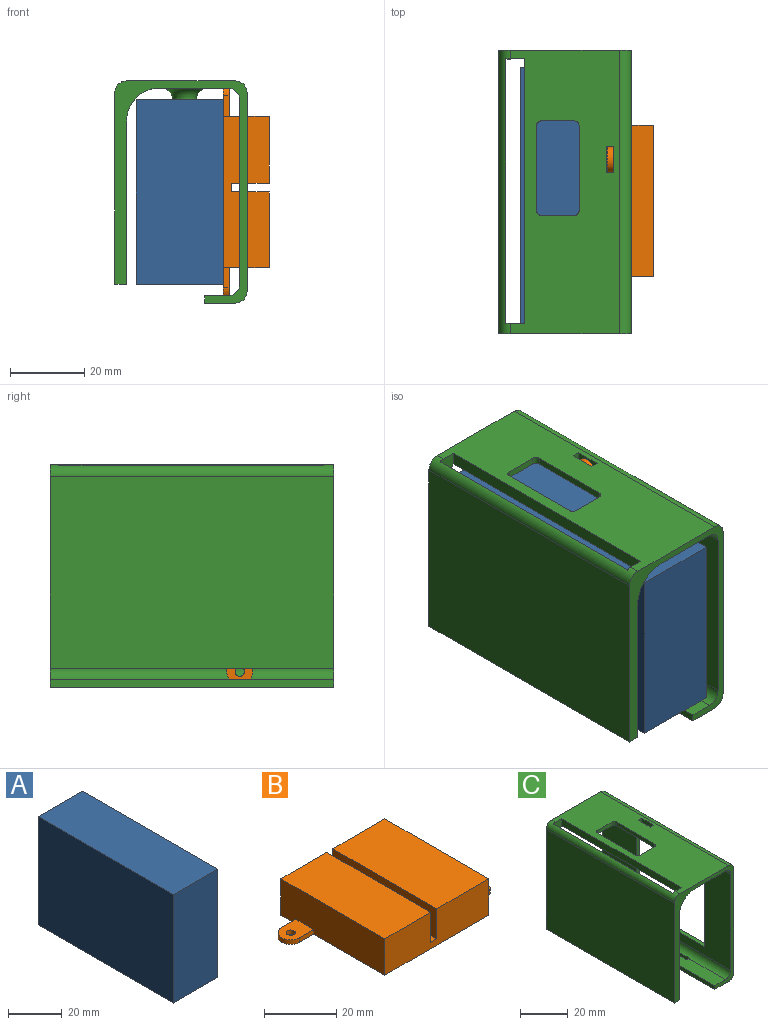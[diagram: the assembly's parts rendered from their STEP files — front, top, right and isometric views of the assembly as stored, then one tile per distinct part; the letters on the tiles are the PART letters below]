
ASSEMBLY  parts=3 mates=6
PART A: 6 faces, bbox 23.5x71.5x49.5 mm
  f0: plane 71.5x23.5mm, normal (0,0,-1), area 1679.9mm2, adj f1,f3,f4,f5
  f1: plane 71.5x49.53mm, normal (1,0,0), area 3541.4mm2, adj f0,f2,f4,f5
  f2: plane 71.5x23.5mm, normal (0,0,1), area 1679.9mm2, adj f1,f3,f4,f5
  f3: plane 71.5x49.53mm, normal (-1,0,0), area 3541.4mm2, adj f0,f2,f4,f5
  f4: plane 49.53x23.5mm, normal (0,-1,0), area 1163.7mm2, adj f0,f1,f2,f3
  f5: plane 49.53x23.5mm, normal (0,1,0), area 1163.7mm2, adj f0,f1,f2,f3
PART B: 20 faces, bbox 58.5x40.6x12.3 mm
  f0: plane 40.64x20.32mm, normal (0,0,1), area 825.8mm2, adj f1,f2,f3,f16
  f1: plane 40.64x12.32mm, normal (0,-1,0), area 476.7mm2, adj f0,f2,f4,f5,f6,f15,f16,f17
  f2: plane 40.64x12.32mm, normal (1,0,0), area 490mm2, adj f0,f1,f3,f6,f7,f8,f10
  f3: plane 40.64x12.32mm, normal (0,1,0), area 476.7mm2, adj f0,f2,f4,f5,f6,f15,f16,f17
  f4: plane 40.64x12.32mm, normal (-1,0,0), area 490mm2, adj f1,f3,f5,f6,f12,f13,f14
  f5: plane 40.64x17.96mm, normal (0,0,1), area 729.9mm2, adj f1,f3,f4,f15
  f6: plane 58.55x40.64mm, normal (0,0,-1), area 1756.1mm2, adj f1,f2,f3,f4,f7,f8,f9,f11
  f7: plane 5.4x1.52mm, normal (0,-1,0), area 8.2mm2, adj f2,f6,f9,f10
  f8: plane 5.4x1.52mm, normal (0,1,0), area 8.2mm2, adj f2,f6,f9,f10
  f9: cylinder r=3.49mm len=6.99mm, axis (0,0,-1), area 16.7mm2, adj f6,f7,f8,f10
  f10: plane 8.89x6.99mm, normal (0,0,1), area 51.8mm2, adj f2,f7,f8,f9,f19
  f11: cylinder r=3.49mm len=6.99mm, axis (0,0,-1), area 16.7mm2, adj f6,f12,f13,f14
  f12: plane 5.52x1.52mm, normal (0,1,0), area 8.4mm2, adj f4,f6,f11,f14
  f13: plane 5.52x1.52mm, normal (0,-1,0), area 8.4mm2, adj f4,f6,f11,f14
  f14: plane 9.02x6.99mm, normal (0,0,1), area 52.7mm2, adj f4,f11,f12,f13,f18
  f15: plane 40.64x10.16mm, normal (1,0,0), area 412.9mm2, adj f1,f3,f5,f17
  f16: plane 40.64x10.16mm, normal (-1,0,0), area 412.9mm2, adj f0,f1,f3,f17
  f17: plane 40.64x2.36mm, normal (0,0,1), area 95.9mm2, adj f1,f3,f15,f16
  f18: cylinder r=1.27mm len=2.54mm, axis (0,0,1), area 12.2mm2, adj f6,f14
  f19: cylinder r=1.27mm len=2.54mm, axis (0,0,1), area 12.2mm2, adj f6,f10
PART C: 46 faces, bbox 35.6x79.2x59.7 mm
  f0: plane 76.2x18.42mm, normal (0,0,-1), area 1024.5mm2, adj f5,f12,f13,f14,f15,f16,f24,f28
  f1: plane 71.12x54.35mm, normal (1,0,0), area 3865mm2, adj f3,f9,f40,f41
  f2: plane 76.2x29.21mm, normal (0,0,1), area 1651.7mm2, adj f3,f12,f13,f14,f15,f16,f17,f26
  f3: cylinder r=3.17mm len=76.2mm, axis (0,-1,0), area 287.1mm2, adj f1,f2,f8,f12,f13,f40,f41
  f4: plane 76.2x8.26mm, normal (0,0,-1), area 617.4mm2, adj f11,f12,f13,f25,f36,f37,f38,f39
  f5: cylinder r=3.17mm len=76.2mm, axis (0,1,0), area 376.7mm2, adj f0,f7,f12,f13,f32,f34,f35
  f6: plane 76.2x53.34mm, normal (1,0,0), area 2412.9mm2, adj f12,f13,f18,f19,f20,f21,f25,f26
  f7: plane 76.2x49.53mm, normal (-1,0,0), area 2122.6mm2, adj f5,f12,f13,f18,f19,f20,f21,f27
  f8: plane 76.2x51.44mm, normal (-1,0,0), area 3919.3mm2, adj f3,f9,f12,f13
  f9: plane 76.2x3.18mm, normal (0,0,-1), area 151.6mm2, adj f1,f8,f12,f13,f40,f41,f43,f44
  f10: plane 76.2x6.35mm, normal (0,0,1), area 474.2mm2, adj f11,f12,f13,f27,f36,f37,f39
  f11: plane 76.2x1.91mm, normal (-1,0,0), area 145.2mm2, adj f4,f10,f12,f13
  f12: plane 59.69x35.56mm, normal (0,1,0), area 378.1mm2, adj f0,f2,f3,f4,f5,f6,f7,f8
  f13: plane 59.69x35.56mm, normal (0,-1,0), area 378.1mm2, adj f0,f2,f3,f4,f5,f6,f7,f8
  f14: plane 8.89x1.93mm, normal (0,1,0), area 16.9mm2, adj f0,f2,f28,f31,f45
  f15: plane 22.86x1.91mm, normal (-1,0,0), area 43.5mm2, adj f0,f2,f28,f29
  f16: plane 8.89x1.93mm, normal (0,-1,0), area 16.9mm2, adj f0,f2,f29,f30,f45
  f17: plane 22.86x2.11mm, normal (1,0,0), area 48.3mm2, adj f2,f30,f31,f45
  f18: plane 40.64x1.91mm, normal (0,0,1), area 77.4mm2, adj f6,f7,f19,f21
  f19: plane 40.64x1.91mm, normal (0,-1,0), area 77.4mm2, adj f6,f7,f18,f20
  f20: plane 40.64x1.91mm, normal (0,0,-1), area 77.4mm2, adj f6,f7,f19,f21
  f21: plane 40.64x1.91mm, normal (0,1,0), area 77.4mm2, adj f6,f7,f18,f20
  f22: cylinder r=3.17mm len=6.35mm, axis (0,0,1), area 12.7mm2, adj f23,f24
  f23: plane 6.35x6.35mm, normal (0,0,-1), area 31.7mm2, adj f22
  f24: torus R=6.35mm, axis (0,0,1), area 135.6mm2, adj f0,f22
  f25: cylinder r=3.17mm len=76.2mm, axis (0,-1,0), area 380mm2, adj f4,f6,f12,f13
  f26: cylinder r=3.17mm len=76.2mm, axis (0,1,0), area 380mm2, adj f2,f6,f12,f13
  f27: cylinder r=3.17mm len=76.2mm, axis (0,-1,0), area 378.1mm2, adj f7,f10,f12,f13,f37,f38,f39
  f28: cylinder r=1.27mm len=1.91mm, axis (0,0,1), area 3.8mm2, adj f0,f2,f14,f15
  f29: cylinder r=1.27mm len=1.91mm, axis (0,0,-1), area 3.8mm2, adj f0,f2,f15,f16
  f30: cylinder r=1.27mm len=2.11mm, axis (0,0,1), area 4.1mm2, adj f2,f16,f17,f45
  f31: cylinder r=1.27mm len=2.11mm, axis (0,0,-1), area 4.1mm2, adj f2,f14,f17,f45
  f32: plane 2.03x1.94mm, normal (0,1,0), area 3.9mm2, adj f0,f2,f5,f33,f34
  f33: plane 6.99x1.91mm, normal (1,0,0), area 13.3mm2, adj f0,f2,f32,f35
  f34: plane 6.99x1.94mm, normal (-1,0,0), area 13.6mm2, adj f2,f5,f32,f35
  f35: plane 2.03x1.94mm, normal (0,-1,0), area 3.9mm2, adj f0,f2,f5,f33,f34
  f36: plane 6.99x1.91mm, normal (1,0,0), area 13.3mm2, adj f4,f10,f37,f39
  f37: plane 1.92x1.66mm, normal (0,-1,0), area 3.2mm2, adj f4,f10,f27,f36,f38
  f38: plane 6.99x1.92mm, normal (-1,0,0), area 13.4mm2, adj f4,f27,f37,f39
  f39: plane 1.92x1.66mm, normal (0,1,0), area 3.2mm2, adj f4,f10,f27,f36,f38
  f40: plane 54.61x5.08mm, normal (0,-1,0), area 90.9mm2, adj f1,f2,f3,f9,f42,f44,f45
  f41: plane 54.61x5.08mm, normal (0,1,0), area 90.9mm2, adj f1,f2,f3,f9,f42,f43,f45
  f42: plane 71.12x3.5mm, normal (-1,0,0), area 248.9mm2, adj f2,f40,f41,f45
  f43: plane 43.82x2.74mm, normal (1,0,0), area 120mm2, adj f9,f13,f41,f45
  f44: plane 43.82x2.34mm, normal (1,0,0), area 102.6mm2, adj f9,f12,f40,f45
  f45: cylinder r=8.89mm len=76.2mm, axis (0,-1,0), area 407.4mm2, adj f0,f12,f13,f14,f16,f17,f30,f31
PLACE A t=(-1.27,35.75,0)mm
PLACE B rot(axis=(0,1,0),90deg) t=(10.48,0,0)mm
PLACE C at identity fixed
MATE planar B.f1 <-> C.f21  axis (0,-1,0) through (22.8,-20.32,11.34)mm
MATE planar A.f4 <-> C.f13  axis (0,-1,0) through (-1.27,-35.75,0)mm
MATE planar A.f0 <-> C.f9  axis (0,0,-1) through (-1.27,0,-24.77)mm
MATE planar A.f1 <-> B.f6  axis (1,0,0) through (10.48,0,0)mm
MATE planar A.f0 <-> A.f0  axis (0,0,-1) through (-1.27,0,-24.77)mm
MATE planar B.f4 <-> C.f20  axis (0,0,1) through (16.75,-0.24,20.32)mm
